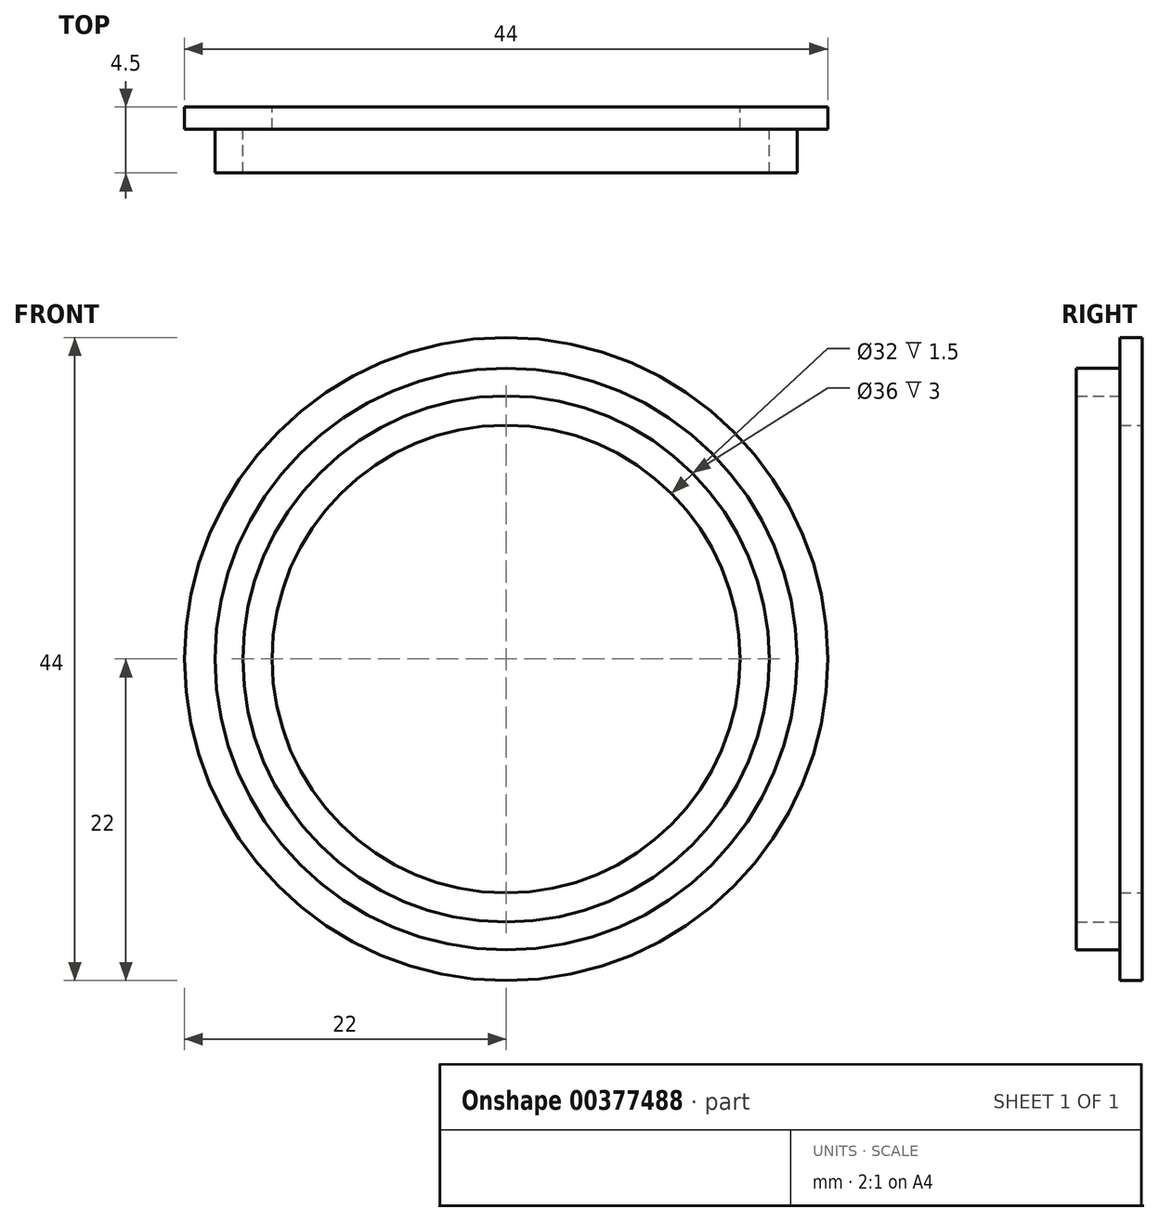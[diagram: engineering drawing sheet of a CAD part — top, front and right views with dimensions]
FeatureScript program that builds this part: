
annotation { "Feature Type Name" : "Feature", "Feature Type Description" : "" }
export const myFeature = defineFeature(function(context is Context, id is Id, definition is map)
    precondition{}
    {
        {
            var Q0;
            Q0=qCreatedBy(makeId("Front.planeOp"),FACE);
            var sketch = newSketch(context, id + "F0", { "sketchPlane" : qUnion([Q0])});
            skCircle(sketch, "E0", {"center": v(0, 0) * mm, "radius": 22 * mm});
            skCircle(sketch, "E1", {"center": v(0, 0) * mm, "radius": 16 * mm});
            skSolve(sketch);
        }
        {
            var Q0;
            Q0=makeQuery(id+"F0.imprint","IMPRINT",FACE,{"disambiguationData":[TD([[makeQuery(id+"F0.imprint","IMPRINT",EDGE,{"derivedFrom":sQuery(id+"F0.wireOp",EDGE,"E0")}),1.0]])]});
            var Q1;
            Q1=makeQuery(id+"F0.imprint","IMPRINT",FACE,{"disambiguationData":[TD([[makeQuery(id+"F0.imprint","IMPRINT",EDGE,{"derivedFrom":sQuery(id+"F0.wireOp",EDGE,"IDzg3WK1-tLJr-dH8J-RCwg-c0Z7R8mAJmQw")}),1.0]])]});
            extrude(context, id + "F1", {"entities" : qUnion([Q0, Q1]), "depth" : 1.5 * mm});
        }
        {
            var Q0;
            Q0=makeQuery(id+"F1.opExtrude","CAP_FACE",FACE,{"disambiguationData":[OSD([sQuery(id+"F0.wireOp",EDGE,"E0"),sQuery(id+"F0.wireOp",EDGE,"E1")])],"isStart":false});
            var sketch = newSketch(context, id + "F2", { "sketchPlane" : qUnion([Q0])});
            skCircle(sketch, "E2", {"center": v(0, 0) * mm, "radius": 19.9 * mm});
            skCircle(sketch, "E3", {"center": v(0, 0) * mm, "radius": 18 * mm});
            skSolve(sketch);
        }
        {
            var Q0;
            Q0 = qSketchRegion(id + "F2", true);
            extrude(context, id + "F3", {"entities" : qUnion([Q0]), "operationType" : NewBodyOperationType.ADD, "depth" : 3 * mm});
        }
    });
